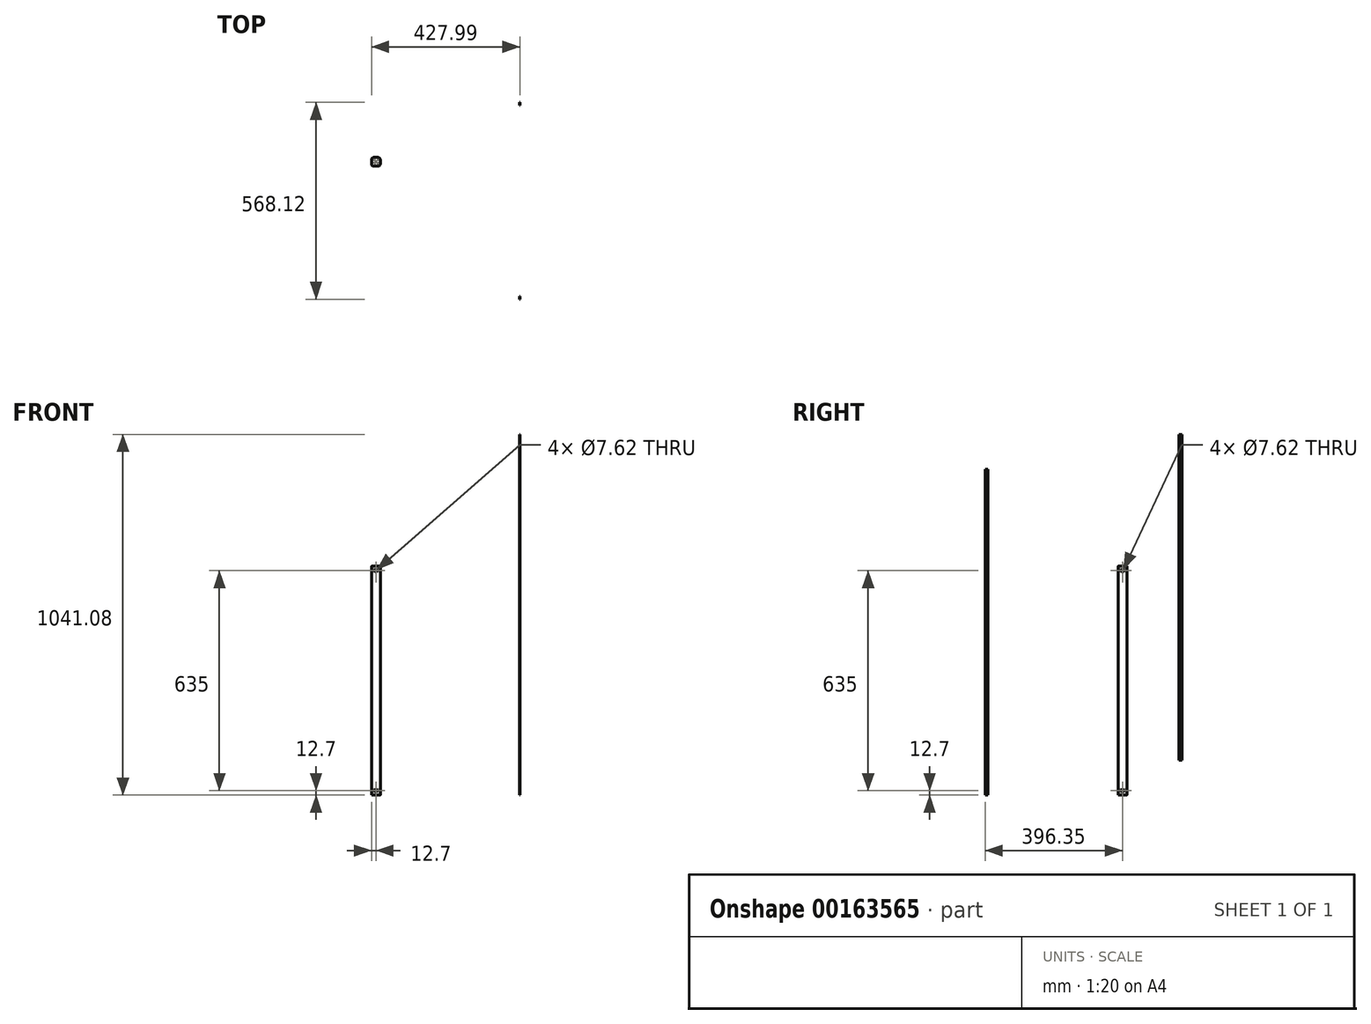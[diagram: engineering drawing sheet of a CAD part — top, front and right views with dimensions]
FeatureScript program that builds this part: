
annotation { "Feature Type Name" : "Feature", "Feature Type Description" : "" }
export const myFeature = defineFeature(function(context is Context, id is Id, definition is map)
    precondition{}
    {
        {
            var Q0;
            Q0=qCreatedBy(makeId("Top.planeOp"),FACE);
            var sketch = newSketch(context, id + "F0", { "sketchPlane" : qUnion([Q0])});
            skLineSegment(sketch, "E0.bottom", {"start": v(6.35, 12.7) * mm, "end": v(-6.35, 12.7) * mm});
            skLineSegment(sketch, "E0.top", {"start": v(6.35, -12.7) * mm, "end": v(-6.35, -12.7) * mm});
            skLineSegment(sketch, "E0.left", {"start": v(12.7, 6.35) * mm, "end": v(12.7, -6.35) * mm});
            skLineSegment(sketch, "E0.right", {"start": v(-12.7, 6.35) * mm, "end": v(-12.7, -6.35) * mm});
            skPoint(sketch, "E0.middle", {"position": v(0, 0) * mm});
            skPoint(sketch, "E1.visualSharp", {"position": v(-12.7, 12.7) * mm});
            skArc(sketch, "E1.filletArc", {"start": v(-6.35, 12.7) * mm, "mid": v(-10.84, 10.84) * mm, "end": v(-12.7, 6.35) * mm});
            skPoint(sketch, "E2.visualSharp", {"position": v(-12.7, -12.7) * mm});
            skArc(sketch, "E2.filletArc", {"start": v(-12.7, -6.35) * mm, "mid": v(-10.84, -10.84) * mm, "end": v(-6.35, -12.7) * mm});
            skPoint(sketch, "E3.visualSharp", {"position": v(12.7, -12.7) * mm});
            skArc(sketch, "E3.filletArc", {"start": v(6.35, -12.7) * mm, "mid": v(10.84, -10.84) * mm, "end": v(12.7, -6.35) * mm});
            skPoint(sketch, "E4.visualSharp", {"position": v(12.7, 12.7) * mm});
            skArc(sketch, "E4.filletArc", {"start": v(12.7, 6.35) * mm, "mid": v(10.84, 10.84) * mm, "end": v(6.35, 12.7) * mm});
            skSolve(sketch);
        }
        {
            var Q0;
            Q0=qSketchRegion(id+"F0",true);
            extrude(context, id + "F1", {"entities" : qUnion([Q0]), "depth" : 660.4 * mm});
        }
        {
            var Q0;
            Q0=qCreatedBy(makeId("Right.planeOp"),FACE);
            var sketch = newSketch(context, id + "F2", { "sketchPlane" : qUnion([Q0])});
            skLineSegment(sketch, "E5.bottom", {"start": v(-396.35, 939.8) * mm, "end": v(-387.88, 939.8) * mm});
            skLineSegment(sketch, "E5.top", {"start": v(-396.35, 0) * mm, "end": v(-387.88, 0) * mm});
            skLineSegment(sketch, "E5.left", {"start": v(-396.35, 939.8) * mm, "end": v(-396.35, 0) * mm});
            skLineSegment(sketch, "E5.right", {"start": v(-387.88, 939.8) * mm, "end": v(-387.88, 0) * mm});
            skSolve(sketch);
        }
        {
            var Q0;
            Q0=qSketchRegion(id+"F2",true);
            extrude(context, id + "F3", {"entities" : qUnion([Q0]), "depth" : 1.27 * mm});
        }
        {
            var Q0;
            Q0=qCreatedBy(makeId("Right.planeOp"),FACE);
            var sketch = newSketch(context, id + "F4", { "sketchPlane" : qUnion([Q0])});
            skLineSegment(sketch, "E6.bottom", {"start": v(163.3, 1041.08) * mm, "end": v(171.77, 1041.08) * mm});
            skLineSegment(sketch, "E6.top", {"start": v(163.3, 101.28) * mm, "end": v(171.77, 101.28) * mm});
            skLineSegment(sketch, "E6.left", {"start": v(163.3, 1041.08) * mm, "end": v(163.3, 101.28) * mm});
            skLineSegment(sketch, "E6.right", {"start": v(171.77, 1041.08) * mm, "end": v(171.77, 101.28) * mm});
            skSolve(sketch);
        }
        {
            var Q0;
            Q0=qSketchRegion(id+"F4",true);
            extrude(context, id + "F5", {"entities" : qUnion([Q0]), "depth" : 1.27 * mm});
        }
        {
            var Q0;
            Q0=makeQuery(id+"F5.opExtrude","SWEPT_BODY",BODY,{"disambiguationData":[OSD([sQuery(id+"F4.wireOp",EDGE,"E6.bottom"),sQuery(id+"F4.wireOp",EDGE,"E6.top"),sQuery(id+"F4.wireOp",EDGE,"E6.left"),sQuery(id+"F4.wireOp",EDGE,"E6.right")])]});
            var Q1;
            Q1=makeQuery(id+"F3.opExtrude","SWEPT_BODY",BODY,{"disambiguationData":[OSD([sQuery(id+"F2.wireOp",EDGE,"E5.bottom"),sQuery(id+"F2.wireOp",EDGE,"E5.top"),sQuery(id+"F2.wireOp",EDGE,"E5.left"),sQuery(id+"F2.wireOp",EDGE,"E5.right")])]});
            transform(context, id + "F6", {"entities" : qUnion([Q0, Q1]), "transformType" : TransformType.TRANSLATION_3D, "dx" : 414.02 * mm, "dy" : 0 * mm, "dz" : 0 * mm, "makeCopy" : false});
        }
        {
            var Q0;
            Q0=makeQuery(id+"F1.opExtrude","SWEPT_FACE",FACE,{"disambiguationData":[OSD([sQuery(id+"F0.wireOp",EDGE,"E0.top")])]});
            var sketch = newSketch(context, id + "F7", { "sketchPlane" : qUnion([Q0])});
            skCircle(sketch, "E7", {"center": v(0, 12.7) * mm, "radius": 3.81 * mm});
            skPoint(sketch, "E8.endSnap0", {"position": v(0, 660.4) * mm});
            skCircle(sketch, "E9", {"center": v(0, 647.7) * mm, "radius": 3.81 * mm});
            skSolve(sketch);
        }
        {
            var Q0;
            Q0=makeQuery(id+"F7.imprint","IMPRINT",FACE,{"disambiguationData":[TD([[makeQuery(id+"F7.imprint","IMPRINT",EDGE,{"derivedFrom":sQuery(id+"F7.wireOp",EDGE,"E7")}),1.0]])]});
            var Q1;
            Q1=makeQuery(id+"F7.imprint","IMPRINT",FACE,{"disambiguationData":[TD([[makeQuery(id+"F7.imprint","IMPRINT",EDGE,{"derivedFrom":sQuery(id+"F7.wireOp",EDGE,"E9")}),1.0]])]});
            extrude(context, id + "F8", {"entities" : qUnion([Q0, Q1]), "operationType" : NewBodyOperationType.REMOVE, "oppositeDirection" : true, "depth" : 25.4 * mm});
        }
        {
            var Q0;
            Q0=makeQuery(id+"F1.opExtrude","SWEPT_FACE",FACE,{"disambiguationData":[OSD([sQuery(id+"F0.wireOp",EDGE,"E0.right")])]});
            var sketch = newSketch(context, id + "F9", { "sketchPlane" : qUnion([Q0])});
            skPoint(sketch, "E10.endSnap0", {"position": v(0, 660.4) * mm});
            skCircle(sketch, "E11", {"center": v(0, 647.7) * mm, "radius": 3.81 * mm});
            skPoint(sketch, "E12.endSnap0", {"position": v(0, 0) * mm});
            skCircle(sketch, "E13", {"center": v(0, 12.7) * mm, "radius": 3.81 * mm});
            skSolve(sketch);
        }
        {
            var Q0;
            Q0=makeQuery(id+"F9.imprint","IMPRINT",FACE,{"disambiguationData":[TD([[makeQuery(id+"F9.imprint","IMPRINT",EDGE,{"derivedFrom":sQuery(id+"F9.wireOp",EDGE,"E13")}),1.0]])]});
            var Q1;
            Q1=makeQuery(id+"F9.imprint","IMPRINT",FACE,{"disambiguationData":[TD([[makeQuery(id+"F9.imprint","IMPRINT",EDGE,{"derivedFrom":sQuery(id+"F9.wireOp",EDGE,"E11")}),1.0]])]});
            extrude(context, id + "F10", {"entities" : qUnion([Q0, Q1]), "operationType" : NewBodyOperationType.REMOVE, "oppositeDirection" : true, "depth" : 25.4 * mm});
        }
    });
